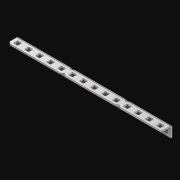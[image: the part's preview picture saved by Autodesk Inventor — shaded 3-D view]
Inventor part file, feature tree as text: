
AUTODESK INVENTOR PART (.ipt)
format: ipt  version: 2021 (Build 250183000, 183)  size: 657,408 bytes
history: native  units: in
note: dims shown in document units (in); Inventor stores cm internally (conversion verified against a paired STEP export)
features: extrude x29, other x28, sketch x3, pattern_linear x1, sheet_metal_op x1
ambient origin geometry x8: Origin, YZ Plane, XZ Plane, XY Plane, X Axis, Y Axis, Z Axis, Center Point
bodies: Solid1 (feature_tree)
feature tree (62):
  pattern_linear  "Rectangular Pattern1"  Spacing1=0.063in  [1 undecoded]
  extrude  "Extrusion1"  Depth=0.5in
  sketch  "Sketch1"  dims[d0=0.182in]
  other  "Srf1"
  sketch  "Sketch2"  dims[d1=0.063in d2=0.0in]
  other  "Srf2"
  other  "Srf3"
  other  "Srf5"
  other  "Srf7"
  other  "Srf9"
  other  "Srf11"
  other  "Srf13"
  other  "Srf15"
  other  "Srf17"
  other  "Srf19"
  other  "Srf21"
  other  "Srf23"
  other  "Srf25"
  other  "Srf27"
  other  "Srf4"
  other  "Srf6"
  other  "Srf8"
  other  "Srf10"
  other  "Srf12"
  other  "Srf14"
  other  "Srf16"
  other  "Srf18"
  other  "Srf20"
  other  "Srf22"
  other  "Srf24"
  other  "Srf26"
  other  "Srf28"
  sketch  "Sketch3"  dims[d3=0.182in d4=0.063in d5=0.0in d8=0.5in d9=10.5in d10=0.0in]
  sheet_metal_op  "Fold1"
  extrude  "ExtrusionSrf1"  Depth=0.5in TaperAngle=0.0deg
  extrude  "ExtrusionSrf2"  [1 undecoded]
  extrude  "ExtrusionSrf3"  [1 undecoded]
  extrude  "ExtrusionSrf4"  [1 undecoded]
  extrude  "ExtrusionSrf5"  [1 undecoded]
  extrude  "ExtrusionSrf6"  [1 undecoded]
  extrude  "ExtrusionSrf7"  [1 undecoded]
  extrude  "ExtrusionSrf8"  [1 undecoded]
  extrude  "ExtrusionSrf9"  [1 undecoded]
  extrude  "ExtrusionSrf10"  [1 undecoded]
  extrude  "ExtrusionSrf11"  [1 undecoded]
  extrude  "ExtrusionSrf12"  [1 undecoded]
  extrude  "ExtrusionSrf13"  [1 undecoded]
  extrude  "ExtrusionSrf14"  [1 undecoded]
  extrude  "ExtrusionSrf15"  [1 undecoded]
  extrude  "ExtrusionSrf37"  [1 undecoded]
  extrude  "ExtrusionSrf38"  [1 undecoded]
  extrude  "ExtrusionSrf39"  [1 undecoded]
  extrude  "ExtrusionSrf40"  [1 undecoded]
  extrude  "ExtrusionSrf41"  [1 undecoded]
  extrude  "ExtrusionSrf42"  [1 undecoded]
  extrude  "ExtrusionSrf43"  [1 undecoded]
  extrude  "ExtrusionSrf44"  [1 undecoded]
  extrude  "ExtrusionSrf45"  [1 undecoded]
  extrude  "ExtrusionSrf46"  [1 undecoded]
  extrude  "ExtrusionSrf47"  [1 undecoded]
  extrude  "ExtrusionSrf48"  [1 undecoded]
  extrude  "ExtrusionSrf49"  [1 undecoded]
note: 28 required parameter values undecoded (feature->parameter linkage not recoverable at this tier; creation-order binding heuristic only, values carry confidence <= 0.55)
